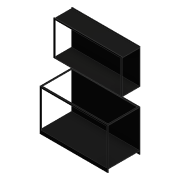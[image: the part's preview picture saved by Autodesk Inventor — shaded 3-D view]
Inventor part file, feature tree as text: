
AUTODESK INVENTOR PART (.ipt)
format: ipt  version: 2016 (Build 200138000, 138)  size: 250,880 bytes
history: native  units: mm
features: extrude x9, projected_geometry x9, sketch x8, plane x1
ambient origin geometry x8: Origin, YZ Plane, XZ Plane, XY Plane, X Axis, Y Axis, Z Axis, Center Point
bodies: Solid1 (feature_tree)
feature tree (27):
  extrude  "Extrusion1"  Depth=10.0mm
  extrude  "Extrusion2"  Depth=80.0mm
  extrude  "Extrusion3"  Depth=30.0mm
  extrude  "Extrusion4"  Depth=30.0mm
  plane  "Work Plane1"
  extrude  "Extrusion5"  Depth=10.0mm
  extrude  "Extrusion9"  Depth=10.0mm
  extrude  "Extrusión10"  Depth=30.0mm
  extrude  "Extrusión11"  TaperAngle=0.0deg  [1 undecoded]
  extrude  "Extrusion13"  Depth=2033.333333mm
  sketch  "Sketch1"  dims[d3=0.0mm d5=10.0mm]
  sketch  "Sketch2"  dims[d6=10.0mm d7=80.0mm]
  projected_geometry  "Projected Loop1"
  sketch  "Sketch3"  dims[d9=0.0mm d10=30.0mm]
  projected_geometry  "Projected Loop2"
  sketch  "Sketch4"  dims[d11=400.0mm d12=0.0mm d13=30.0mm]
  projected_geometry  "Projected Loop3"
  projected_geometry  "Projected Loop4"
  projected_geometry  "Projected Loop5"
  sketch  "Sketch5"  dims[d14=30.0mm d15=10.0mm]
  sketch  "Sketch9"  dims[d16=0.0mm d18=10.0mm]
  projected_geometry  "Projected Loop9"
  sketch  "Boceto10"  dims[d19=0.0mm d32=30.0mm]
  projected_geometry  "Contorno proyectado10"
  projected_geometry  "Contorno proyectado11"
  sketch  "Sketch13"  dims[d33=10.0mm d34=0.0mm d36=2033.333333mm d39=10.0mm d40=10.0mm d41=10.0mm d43=0.0mm d44=30.0mm d45=30.0mm d46=30.0mm d48=750.0mm d49=0.0mm d53=10.0mm d54=20.0mm d55=2033.333333mm d56=0.0mm]
  projected_geometry  "Projected Loop12"
note: 1 required parameter value undecoded (feature->parameter linkage not recoverable at this tier; creation-order binding heuristic only, values carry confidence <= 0.55)
